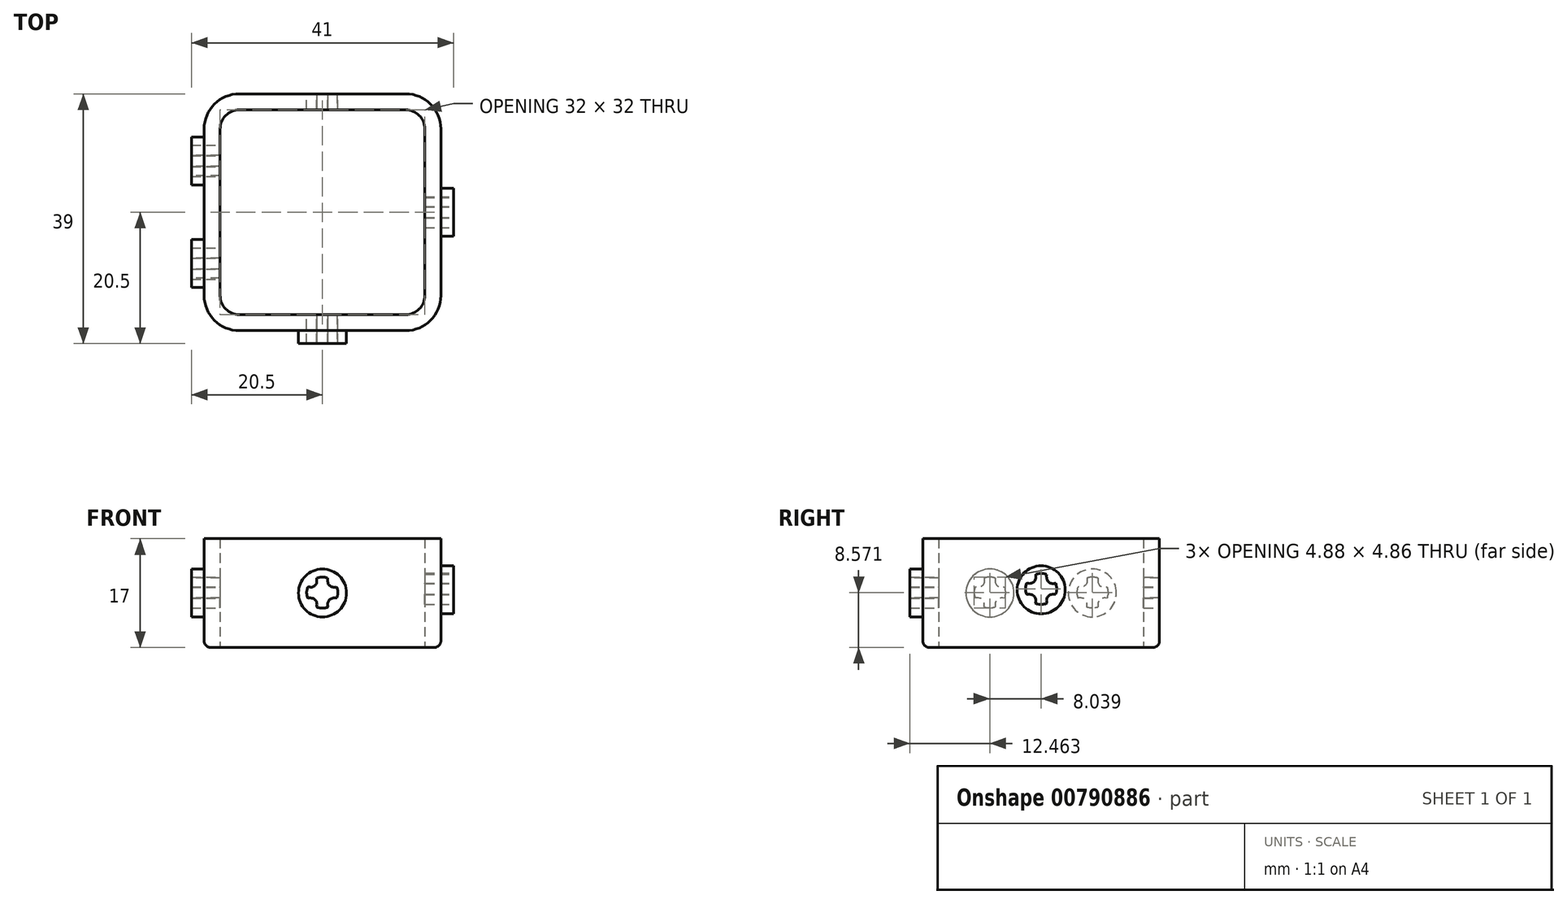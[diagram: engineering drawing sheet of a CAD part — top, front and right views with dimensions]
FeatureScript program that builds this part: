
annotation { "Feature Type Name" : "Feature", "Feature Type Description" : "" }
export const myFeature = defineFeature(function(context is Context, id is Id, definition is map)
    precondition{}
    {
        {
            var Q0;
            Q0=qCreatedBy(makeId("Top.planeOp"),FACE);
            var sketch = newSketch(context, id + "F0", { "sketchPlane" : qUnion([Q0])});
            skLineSegment(sketch, "E0.bottom", {"start": v(-16, 16) * mm, "end": v(16, 16) * mm});
            skLineSegment(sketch, "E0.top", {"start": v(-16, -16) * mm, "end": v(16, -16) * mm});
            skLineSegment(sketch, "E0.left", {"start": v(-16, 16) * mm, "end": v(-16, -16) * mm});
            skLineSegment(sketch, "E0.right", {"start": v(16, 16) * mm, "end": v(16, -16) * mm});
            skPoint(sketch, "E1", {"position": v(-16, 0) * mm});
            skPoint(sketch, "E2", {"position": v(0, 16) * mm});
            skLineSegment(sketch, "E3.bottom", {"start": v(-18.5, 18.5) * mm, "end": v(18.5, 18.5) * mm});
            skLineSegment(sketch, "E3.top", {"start": v(-18.5, -18.5) * mm, "end": v(18.5, -18.5) * mm});
            skLineSegment(sketch, "E3.left", {"start": v(-18.5, 18.5) * mm, "end": v(-18.5, -18.5) * mm});
            skLineSegment(sketch, "E3.right", {"start": v(18.5, 18.5) * mm, "end": v(18.5, -18.5) * mm});
            skSolve(sketch);
        }
        {
            var Q0;
            Q0=makeQuery(id+"F0.imprint","IMPRINT",FACE,{"disambiguationData":[TD([[makeQuery(id+"F0.imprint","IMPRINT",EDGE,{"derivedFrom":sQuery(id+"F0.wireOp",EDGE,"E0.bottom")}),1.0]])]});
            extrude(context, id + "F1", {"entities" : qUnion([Q0]), "depth" : 17 * mm, "offsetDistance" : 25 * mm});
        }
        {
            var Q0;
            Q0=makeQuery(id+"F1.opExtrude","SWEPT_EDGE",EDGE,{"disambiguationData":[OSD([sQuery(id+"F0.wireOp",EDGE,"E0.bottom"),sQuery(id+"F0.wireOp",EDGE,"E0.left")])]});
            var Q1;
            Q1=makeQuery(id+"F1.opExtrude","SWEPT_EDGE",EDGE,{"disambiguationData":[OSD([sQuery(id+"F0.wireOp",EDGE,"E0.bottom"),sQuery(id+"F0.wireOp",EDGE,"E0.right")])]});
            var Q2;
            Q2=makeQuery(id+"F1.opExtrude","SWEPT_EDGE",EDGE,{"disambiguationData":[OSD([sQuery(id+"F0.wireOp",EDGE,"E0.top"),sQuery(id+"F0.wireOp",EDGE,"E0.right")])]});
            var Q3;
            Q3=makeQuery(id+"F1.opExtrude","SWEPT_EDGE",EDGE,{"disambiguationData":[OSD([sQuery(id+"F0.wireOp",EDGE,"E0.top"),sQuery(id+"F0.wireOp",EDGE,"E0.left")])]});
            fillet(context, id + "F2", {"entities" : qUnion([Q0, Q1, Q2, Q3]), "radius" : 3 * mm, "tangentPropagation" : true, "allowEdgeOverflow" : false});
        }
        {
            var Q0;
            Q0=makeQuery(id+"F1.opExtrude","SWEPT_FACE",FACE,{"disambiguationData":[OSD([sQuery(id+"F0.wireOp",EDGE,"E3.left")])]});
            var sketch = newSketch(context, id + "F3", { "sketchPlane" : qUnion([Q0])});
            skCircle(sketch, "E4", {"center": v(-8, 8.5) * mm, "radius": 3.75 * mm});
            skCircle(sketch, "E5", {"center": v(8, 8.5) * mm, "radius": 3.75 * mm});
            skLineSegment(sketch, "E6", {"start": v(-8, 8.5) * mm, "end": v(8, 8.5) * mm});
            skPoint(sketch, "E7", {"position": v(0, 8.5) * mm});
            skSolve(sketch);
        }
        {
            var Q0;
            Q0=makeQuery(id+"F3.imprint","IMPRINT",FACE,{"disambiguationData":[TD([[makeQuery(id+"F3.imprint","IMPRINT",EDGE,{"derivedFrom":sQuery(id+"F3.wireOp",EDGE,"E4")}),1.0]])]});
            var Q1;
            Q1=makeQuery(id+"F3.imprint","IMPRINT",FACE,{"disambiguationData":[TD([[makeQuery(id+"F3.imprint","IMPRINT",EDGE,{"derivedFrom":sQuery(id+"F3.wireOp",EDGE,"ysG9YYlj-4qmX-fUi1-GXW1-Whetp2Y7ZTwk")}),1.0]])]});
            var Q2;
            Q2=makeQuery(id+"F3.imprint","IMPRINT",FACE,{"disambiguationData":[TD([[makeQuery(id+"F3.imprint","IMPRINT",EDGE,{"derivedFrom":sQuery(id+"F3.wireOp",EDGE,"E5")}),1.0]])]});
            extrude(context, id + "F4", {"entities" : qUnion([Q0, Q1, Q2]), "operationType" : NewBodyOperationType.ADD, "depth" : 2 * mm, "offsetDistance" : 25 * mm});
        }
        {
            var Q0;
            Q0=makeQuery(id+"F1.opExtrude","SWEPT_FACE",FACE,{"disambiguationData":[OSD([sQuery(id+"F0.wireOp",EDGE,"E3.top")])]});
            var sketch = newSketch(context, id + "F5", { "sketchPlane" : qUnion([Q0])});
            skCircle(sketch, "E8", {"center": v(0, 8.5) * mm, "radius": 3.75 * mm});
            skSolve(sketch);
        }
        {
            var Q0;
            Q0=makeQuery(id+"F5.imprint","IMPRINT",FACE,{"disambiguationData":[TD([[makeQuery(id+"F5.imprint","IMPRINT",EDGE,{"derivedFrom":sQuery(id+"F5.wireOp",EDGE,"E8")}),1.0]])]});
            extrude(context, id + "F6", {"entities" : qUnion([Q0]), "operationType" : NewBodyOperationType.ADD, "depth" : 2 * mm, "offsetDistance" : 25 * mm});
        }
        {
            var Q0;
            Q0=makeQuery(id+"F6.opExtrude","CAP_FACE",FACE,{"disambiguationData":[OSD([sQuery(id+"F5.wireOp",EDGE,"E8")])],"isStart":false});
            var sketch = newSketch(context, id + "F7", { "sketchPlane" : qUnion([Q0])});
            skFitSpline(sketch, "E9", {"points": [v(-0.88, 10.83) * mm, v(0, 11) * mm, v(0.82, 10.83) * mm], "startDerivative": vector(1.75, 0.5) * mm, "endDerivative": vector(1.65, -0.5) * mm});
            skFitSpline(sketch, "E10", {"points": [v(0.82, 10.83) * mm, v(0.82, 10.27) * mm, v(0.97, 9.83) * mm, v(1.28, 9.54) * mm, v(1.62, 9.42) * mm, v(2.04, 9.41) * mm, v(2.24, 9.41) * mm, v(2.32, 9.17) * mm, v(2.4, 8.78) * mm, v(2.4, 8.44) * mm, v(2.36, 8.13) * mm, v(2.24, 7.71) * mm], "startDerivative": vector(-0.26, -5.18) * mm, "endDerivative": vector(-1.41, -4.37) * mm});
            skFitSpline(sketch, "E11", {"points": [v(-0.88, 10.83) * mm, v(-0.88, 10.54) * mm, v(-0.88, 10.3) * mm, v(-0.91, 10.1) * mm, v(-1.08, 9.76) * mm, v(-1.28, 9.58) * mm, v(-1.54, 9.45) * mm, v(-1.86, 9.41) * mm, v(-2.3, 9.41) * mm, v(-2.4, 9.13) * mm, v(-2.45, 8.85) * mm, v(-2.47, 8.52) * mm, v(-2.44, 8.23) * mm, v(-2.38, 7.96) * mm, v(-2.3, 7.71) * mm, v(-2.1, 7.71) * mm, v(-1.8, 7.71) * mm, v(-1.55, 7.68) * mm, v(-1.36, 7.6) * mm, v(-1.13, 7.42) * mm, v(-1.03, 7.28) * mm, v(-0.94, 7.1) * mm, v(-0.88, 6.86) * mm, v(-0.88, 6.6) * mm, v(-0.88, 6.3) * mm, v(-0.63, 6.21) * mm, v(-0.28, 6.15) * mm, v(0, 6.14) * mm, v(0.27, 6.16) * mm, v(0.63, 6.23) * mm, v(0.82, 6.3) * mm, v(0.82, 6.6) * mm, v(0.82, 6.89) * mm, v(0.92, 7.22) * mm, v(1.06, 7.41) * mm, v(1.33, 7.61) * mm, v(1.74, 7.71) * mm, v(2.24, 7.71) * mm], "startDerivative": vector(-0.02, -10.87) * mm, "endDerivative": vector(14.17, -0.52) * mm});
            skLineSegment(sketch, "E12", {"start": v(0, 11) * mm, "end": v(0, 6.14) * mm});
            skPoint(sketch, "E13", {"position": v(0, 8.57) * mm});
            skPoint(sketch, "E14", {"position": v(0, 8.36) * mm});
            skLineSegment(sketch, "E15", {"start": v(-2.47, 8.52) * mm, "end": v(2.42, 8.52) * mm});
            skSolve(sketch);
        }
        {
            var Q0;
            {var subQ0=sQuery(id+"F7.wireOp",EDGE,"E11");var subQ1=sQuery(id+"F7.wireOp",EDGE,"E9");var subQ2=makeQuery(id+"F7.imprint","INTERSECT",VERTEX,{"derivedFrom":[subQ1,subQ0]});Q0=makeQuery(id+"F7.imprint","IMPRINT",FACE,{"disambiguationData":[TD([[makeQuery(id+"F7.imprint","IMPRINT",EDGE,{"disambiguationData":[TD([[subQ2,-1.0]])],"derivedFrom":subQ1}),-1.0]])]});}
            var Q1;
            {var subQ0=sQuery(id+"F7.wireOp",EDGE,"E10");var subQ1=sQuery(id+"F7.wireOp",EDGE,"E9");var subQ2=makeQuery(id+"F7.imprint","INTERSECT",VERTEX,{"derivedFrom":[subQ1,subQ0]});Q1=makeQuery(id+"F7.imprint","IMPRINT",FACE,{"disambiguationData":[TD([[makeQuery(id+"F7.imprint","IMPRINT",EDGE,{"disambiguationData":[TD([[subQ2,1.0]])],"derivedFrom":subQ1}),-1.0]])]});}
            var Q2;
            {var subQ0=sQuery(id+"F7.wireOp",EDGE,"E11");var subQ1=sQuery(id+"F7.wireOp",EDGE,"E10");var subQ2=makeQuery(id+"F7.imprint","INTERSECT",VERTEX,{"derivedFrom":[subQ1,subQ0]});Q2=makeQuery(id+"F7.imprint","IMPRINT",FACE,{"disambiguationData":[TD([[makeQuery(id+"F7.imprint","IMPRINT",EDGE,{"disambiguationData":[TD([[subQ2,1.0]])],"derivedFrom":subQ1}),-1.0]])]});}
            var Q3;
            {var subQ0=sQuery(id+"F7.wireOp",EDGE,"E12");var subQ1=sQuery(id+"F7.wireOp",EDGE,"E11");var subQ2=makeQuery(id+"F7.imprint","INTERSECT",VERTEX,{"derivedFrom":[subQ1,subQ0]});Q3=makeQuery(id+"F7.imprint","IMPRINT",FACE,{"disambiguationData":[TD([[makeQuery(id+"F7.imprint","IMPRINT",EDGE,{"disambiguationData":[TD([[subQ2,1.0]])],"derivedFrom":subQ1}),1.0]])]});}
            extrude(context, id + "F8", {"entities" : qUnion([Q0, Q1, Q2, Q3]), "operationType" : NewBodyOperationType.REMOVE, "oppositeDirection" : true, "depth" : 43.1 * mm, "offsetDistance" : 25 * mm});
        }
        {
            var Q0;
            Q0=makeQuery(id+"F1.opExtrude","SWEPT_EDGE",EDGE,{"disambiguationData":[OSD([sQuery(id+"F0.wireOp",EDGE,"E3.top"),sQuery(id+"F0.wireOp",EDGE,"E3.left")])]});
            var Q1;
            Q1=makeQuery(id+"F1.opExtrude","SWEPT_EDGE",EDGE,{"disambiguationData":[OSD([sQuery(id+"F0.wireOp",EDGE,"E3.top"),sQuery(id+"F0.wireOp",EDGE,"E3.right")])]});
            var Q2;
            Q2=makeQuery(id+"F1.opExtrude","SWEPT_EDGE",EDGE,{"disambiguationData":[OSD([sQuery(id+"F0.wireOp",EDGE,"E3.bottom"),sQuery(id+"F0.wireOp",EDGE,"E3.right")])]});
            var Q3;
            Q3=makeQuery(id+"F1.opExtrude","SWEPT_EDGE",EDGE,{"disambiguationData":[OSD([sQuery(id+"F0.wireOp",EDGE,"E3.bottom"),sQuery(id+"F0.wireOp",EDGE,"E3.left")])]});
            fillet(context, id + "F9", {"entities" : qUnion([Q0, Q1, Q2, Q3]), "radius" : 5.5 * mm, "tangentPropagation" : true, "allowEdgeOverflow" : false});
        }
        {
            var Q0;
            Q0=makeQuery(id+"F1.opExtrude","CAP_EDGE",EDGE,{"disambiguationData":[OSD([sQuery(id+"F0.wireOp",EDGE,"E3.right")])],"isStart":true});
            var Q1;
            {var subQ0=sQuery(id+"F0.wireOp",EDGE,"E3.left");var subQ1=sQuery(id+"F0.wireOp",EDGE,"E3.top");Q1=makeQuery(id+"F9.opFillet","BLEND_EDGE",EDGE,{"blendedFrom":[makeQuery(id+"F1.opExtrude","SWEPT_EDGE",EDGE,{"disambiguationData":[OSD([subQ1,subQ0])]}),makeQuery(id+"F1.opExtrude","CAP_FACE",FACE,{"disambiguationData":[OSD([sQuery(id+"F0.wireOp",EDGE,"E0.bottom"),sQuery(id+"F0.wireOp",EDGE,"E0.top"),sQuery(id+"F0.wireOp",EDGE,"E0.left"),sQuery(id+"F0.wireOp",EDGE,"E0.right"),sQuery(id+"F0.wireOp",EDGE,"E3.bottom"),subQ1,subQ0,sQuery(id+"F0.wireOp",EDGE,"E3.right")])],"isStart":true})],"blendedInto":[makeQuery(id+"F1.opExtrude","CAP_FACE",FACE,{"disambiguationData":[OSD([sQuery(id+"F0.wireOp",EDGE,"E0.bottom"),sQuery(id+"F0.wireOp",EDGE,"E0.top"),sQuery(id+"F0.wireOp",EDGE,"E0.left"),sQuery(id+"F0.wireOp",EDGE,"E0.right"),sQuery(id+"F0.wireOp",EDGE,"E3.bottom"),subQ1,subQ0,sQuery(id+"F0.wireOp",EDGE,"E3.right")])],"isStart":true})]});}
            var Q2;
            Q2=makeQuery(id+"F1.opExtrude","CAP_EDGE",EDGE,{"disambiguationData":[OSD([sQuery(id+"F0.wireOp",EDGE,"E3.top")])],"isStart":true});
            var Q3;
            {var subQ0=sQuery(id+"F0.wireOp",EDGE,"E3.right");var subQ1=sQuery(id+"F0.wireOp",EDGE,"E3.top");Q3=makeQuery(id+"F9.opFillet","BLEND_EDGE",EDGE,{"blendedFrom":[makeQuery(id+"F1.opExtrude","SWEPT_EDGE",EDGE,{"disambiguationData":[OSD([subQ1,subQ0])]}),makeQuery(id+"F1.opExtrude","CAP_FACE",FACE,{"disambiguationData":[OSD([sQuery(id+"F0.wireOp",EDGE,"E0.bottom"),sQuery(id+"F0.wireOp",EDGE,"E0.top"),sQuery(id+"F0.wireOp",EDGE,"E0.left"),sQuery(id+"F0.wireOp",EDGE,"E0.right"),sQuery(id+"F0.wireOp",EDGE,"E3.bottom"),subQ1,sQuery(id+"F0.wireOp",EDGE,"E3.left"),subQ0])],"isStart":true})],"blendedInto":[makeQuery(id+"F1.opExtrude","CAP_FACE",FACE,{"disambiguationData":[OSD([sQuery(id+"F0.wireOp",EDGE,"E0.bottom"),sQuery(id+"F0.wireOp",EDGE,"E0.top"),sQuery(id+"F0.wireOp",EDGE,"E0.left"),sQuery(id+"F0.wireOp",EDGE,"E0.right"),sQuery(id+"F0.wireOp",EDGE,"E3.bottom"),subQ1,sQuery(id+"F0.wireOp",EDGE,"E3.left"),subQ0])],"isStart":true})]});}
            var Q4;
            Q4=makeQuery(id+"F1.opExtrude","CAP_EDGE",EDGE,{"disambiguationData":[OSD([sQuery(id+"F0.wireOp",EDGE,"E3.left")])],"isStart":true});
            var Q5;
            {var subQ0=sQuery(id+"F0.wireOp",EDGE,"E3.left");var subQ1=sQuery(id+"F0.wireOp",EDGE,"E3.bottom");Q5=makeQuery(id+"F9.opFillet","BLEND_EDGE",EDGE,{"blendedFrom":[makeQuery(id+"F1.opExtrude","SWEPT_EDGE",EDGE,{"disambiguationData":[OSD([subQ1,subQ0])]}),makeQuery(id+"F1.opExtrude","CAP_FACE",FACE,{"disambiguationData":[OSD([sQuery(id+"F0.wireOp",EDGE,"E0.bottom"),sQuery(id+"F0.wireOp",EDGE,"E0.top"),sQuery(id+"F0.wireOp",EDGE,"E0.left"),sQuery(id+"F0.wireOp",EDGE,"E0.right"),subQ1,sQuery(id+"F0.wireOp",EDGE,"E3.top"),subQ0,sQuery(id+"F0.wireOp",EDGE,"E3.right")])],"isStart":true})],"blendedInto":[makeQuery(id+"F1.opExtrude","CAP_FACE",FACE,{"disambiguationData":[OSD([sQuery(id+"F0.wireOp",EDGE,"E0.bottom"),sQuery(id+"F0.wireOp",EDGE,"E0.top"),sQuery(id+"F0.wireOp",EDGE,"E0.left"),sQuery(id+"F0.wireOp",EDGE,"E0.right"),subQ1,sQuery(id+"F0.wireOp",EDGE,"E3.top"),subQ0,sQuery(id+"F0.wireOp",EDGE,"E3.right")])],"isStart":true})]});}
            var Q6;
            Q6=makeQuery(id+"F1.opExtrude","CAP_EDGE",EDGE,{"disambiguationData":[OSD([sQuery(id+"F0.wireOp",EDGE,"E3.bottom")])],"isStart":true});
            var Q7;
            {var subQ0=sQuery(id+"F0.wireOp",EDGE,"E3.right");var subQ1=sQuery(id+"F0.wireOp",EDGE,"E3.bottom");Q7=makeQuery(id+"F9.opFillet","BLEND_EDGE",EDGE,{"blendedFrom":[makeQuery(id+"F1.opExtrude","SWEPT_EDGE",EDGE,{"disambiguationData":[OSD([subQ1,subQ0])]}),makeQuery(id+"F1.opExtrude","CAP_FACE",FACE,{"disambiguationData":[OSD([sQuery(id+"F0.wireOp",EDGE,"E0.bottom"),sQuery(id+"F0.wireOp",EDGE,"E0.top"),sQuery(id+"F0.wireOp",EDGE,"E0.left"),sQuery(id+"F0.wireOp",EDGE,"E0.right"),subQ1,sQuery(id+"F0.wireOp",EDGE,"E3.top"),sQuery(id+"F0.wireOp",EDGE,"E3.left"),subQ0])],"isStart":true})],"blendedInto":[makeQuery(id+"F1.opExtrude","CAP_FACE",FACE,{"disambiguationData":[OSD([sQuery(id+"F0.wireOp",EDGE,"E0.bottom"),sQuery(id+"F0.wireOp",EDGE,"E0.top"),sQuery(id+"F0.wireOp",EDGE,"E0.left"),sQuery(id+"F0.wireOp",EDGE,"E0.right"),subQ1,sQuery(id+"F0.wireOp",EDGE,"E3.top"),sQuery(id+"F0.wireOp",EDGE,"E3.left"),subQ0])],"isStart":true})]});}
            fillet(context, id + "F10", {"entities" : qUnion([Q0, Q1, Q2, Q3, Q4, Q5, Q6, Q7]), "radius" : 1 * mm, "tangentPropagation" : true, "allowEdgeOverflow" : false});
        }
        {
            var Q0;
            Q0=makeQuery(id+"F4.opExtrude","CAP_FACE",FACE,{"disambiguationData":[OSD([sQuery(id+"F3.wireOp",EDGE,"E4")])],"isStart":false});
            var sketch = newSketch(context, id + "F11", { "sketchPlane" : qUnion([Q0])});
            skFitSpline(sketch, "E16", {"points": [v(-8.86, 10.84) * mm, v(-7.98, 11) * mm, v(-7.16, 10.84) * mm], "startDerivative": vector(1.75, 0.5) * mm, "endDerivative": vector(1.65, -0.5) * mm});
            skFitSpline(sketch, "E17", {"points": [v(-7.16, 10.84) * mm, v(-7.16, 10.27) * mm, v(-7.02, 9.84) * mm, v(-6.7, 9.54) * mm, v(-6.36, 9.42) * mm, v(-5.94, 9.41) * mm, v(-5.74, 9.41) * mm, v(-5.66, 9.17) * mm, v(-5.59, 8.79) * mm, v(-5.58, 8.45) * mm, v(-5.62, 8.13) * mm, v(-5.74, 7.71) * mm], "startDerivative": vector(-0.26, -5.18) * mm, "endDerivative": vector(-1.41, -4.37) * mm});
            skFitSpline(sketch, "E18", {"points": [v(-8.86, 10.84) * mm, v(-8.86, 10.54) * mm, v(-8.87, 10.3) * mm, v(-8.9, 10.1) * mm, v(-9.07, 9.76) * mm, v(-9.26, 9.58) * mm, v(-9.52, 9.45) * mm, v(-9.84, 9.41) * mm, v(-10.29, 9.41) * mm, v(-10.37, 9.14) * mm, v(-10.43, 8.85) * mm, v(-10.45, 8.52) * mm, v(-10.43, 8.23) * mm, v(-10.37, 7.97) * mm, v(-10.29, 7.71) * mm, v(-10.1, 7.71) * mm, v(-9.78, 7.71) * mm, v(-9.53, 7.68) * mm, v(-9.34, 7.6) * mm, v(-9.12, 7.42) * mm, v(-9, 7.28) * mm, v(-8.92, 7.1) * mm, v(-8.87, 6.86) * mm, v(-8.86, 6.61) * mm, v(-8.86, 6.3) * mm, v(-8.6, 6.21) * mm, v(-8.26, 6.15) * mm, v(-7.98, 6.14) * mm, v(-7.72, 6.16) * mm, v(-7.35, 6.23) * mm, v(-7.16, 6.3) * mm, v(-7.16, 6.61) * mm, v(-7.16, 6.89) * mm, v(-7.06, 7.22) * mm, v(-6.92, 7.41) * mm, v(-6.65, 7.62) * mm, v(-6.24, 7.71) * mm, v(-5.74, 7.71) * mm], "startDerivative": vector(-0.02, -10.87) * mm, "endDerivative": vector(14.17, -0.52) * mm});
            skLineSegment(sketch, "E19", {"start": v(-7.98, 11) * mm, "end": v(-7.98, 6.14) * mm});
            skPoint(sketch, "E20", {"position": v(-7.98, 8.57) * mm});
            skPoint(sketch, "E21", {"position": v(-7.98, 8.36) * mm});
            skLineSegment(sketch, "E22", {"start": v(-10.45, 8.52) * mm, "end": v(-5.56, 8.52) * mm});
            skFitSpline(sketch, "E23", {"points": [v(7.19, 10.84) * mm, v(8.07, 11) * mm, v(8.89, 10.84) * mm], "startDerivative": vector(1.75, 0.5) * mm, "endDerivative": vector(1.65, -0.5) * mm});
            skFitSpline(sketch, "E24", {"points": [v(8.89, 10.84) * mm, v(8.89, 10.27) * mm, v(9.04, 9.84) * mm, v(9.35, 9.54) * mm, v(9.7, 9.42) * mm, v(10.1, 9.41) * mm, v(10.3, 9.41) * mm, v(10.39, 9.17) * mm, v(10.46, 8.79) * mm, v(10.47, 8.45) * mm, v(10.43, 8.13) * mm, v(10.3, 7.71) * mm], "startDerivative": vector(-0.26, -5.18) * mm, "endDerivative": vector(-1.41, -4.37) * mm});
            skFitSpline(sketch, "E25", {"points": [v(7.19, 10.84) * mm, v(7.19, 10.54) * mm, v(7.19, 10.3) * mm, v(7.16, 10.1) * mm, v(6.99, 9.76) * mm, v(6.79, 9.58) * mm, v(6.53, 9.45) * mm, v(6.2, 9.41) * mm, v(5.77, 9.41) * mm, v(5.68, 9.14) * mm, v(5.62, 8.85) * mm, v(5.6, 8.52) * mm, v(5.63, 8.23) * mm, v(5.69, 7.97) * mm, v(5.77, 7.71) * mm, v(5.96, 7.71) * mm, v(6.28, 7.71) * mm, v(6.52, 7.68) * mm, v(6.71, 7.6) * mm, v(6.94, 7.42) * mm, v(7.04, 7.28) * mm, v(7.13, 7.1) * mm, v(7.18, 6.86) * mm, v(7.19, 6.61) * mm, v(7.19, 6.3) * mm, v(7.44, 6.21) * mm, v(7.8, 6.15) * mm, v(8.07, 6.14) * mm, v(8.34, 6.16) * mm, v(8.7, 6.23) * mm, v(8.89, 6.3) * mm, v(8.89, 6.61) * mm, v(8.9, 6.89) * mm, v(9, 7.22) * mm, v(9.13, 7.41) * mm, v(9.4, 7.62) * mm, v(9.81, 7.71) * mm, v(10.3, 7.71) * mm], "startDerivative": vector(-0.02, -10.87) * mm, "endDerivative": vector(14.17, -0.52) * mm});
            skLineSegment(sketch, "E26", {"start": v(8.07, 11) * mm, "end": v(8.07, 6.14) * mm});
            skPoint(sketch, "E27", {"position": v(8.07, 8.57) * mm});
            skPoint(sketch, "E28", {"position": v(8.07, 8.36) * mm});
            skLineSegment(sketch, "E29", {"start": v(5.6, 8.52) * mm, "end": v(10.49, 8.52) * mm});
            skSolve(sketch);
        }
        {
            var Q0;
            {var subQ0=sQuery(id+"F11.wireOp",EDGE,"E18");var subQ1=sQuery(id+"F11.wireOp",EDGE,"E16");var subQ2=makeQuery(id+"F11.imprint","INTERSECT",VERTEX,{"derivedFrom":[subQ1,subQ0]});Q0=makeQuery(id+"F11.imprint","IMPRINT",FACE,{"disambiguationData":[TD([[makeQuery(id+"F11.imprint","IMPRINT",EDGE,{"disambiguationData":[TD([[subQ2,-1.0]])],"derivedFrom":subQ1}),-1.0]])]});}
            var Q1;
            {var subQ0=sQuery(id+"F11.wireOp",EDGE,"E17");var subQ1=sQuery(id+"F11.wireOp",EDGE,"E16");var subQ2=makeQuery(id+"F11.imprint","INTERSECT",VERTEX,{"derivedFrom":[subQ1,subQ0]});Q1=makeQuery(id+"F11.imprint","IMPRINT",FACE,{"disambiguationData":[TD([[makeQuery(id+"F11.imprint","IMPRINT",EDGE,{"disambiguationData":[TD([[subQ2,1.0]])],"derivedFrom":subQ1}),-1.0]])]});}
            var Q2;
            {var subQ0=sQuery(id+"F11.wireOp",EDGE,"E18");var subQ1=sQuery(id+"F11.wireOp",EDGE,"E17");var subQ2=makeQuery(id+"F11.imprint","INTERSECT",VERTEX,{"derivedFrom":[subQ1,subQ0]});Q2=makeQuery(id+"F11.imprint","IMPRINT",FACE,{"disambiguationData":[TD([[makeQuery(id+"F11.imprint","IMPRINT",EDGE,{"disambiguationData":[TD([[subQ2,1.0]])],"derivedFrom":subQ1}),-1.0]])]});}
            var Q3;
            {var subQ0=sQuery(id+"F11.wireOp",EDGE,"E19");var subQ1=sQuery(id+"F11.wireOp",EDGE,"E18");var subQ2=makeQuery(id+"F11.imprint","INTERSECT",VERTEX,{"derivedFrom":[subQ1,subQ0]});Q3=makeQuery(id+"F11.imprint","IMPRINT",FACE,{"disambiguationData":[TD([[makeQuery(id+"F11.imprint","IMPRINT",EDGE,{"disambiguationData":[TD([[subQ2,1.0]])],"derivedFrom":subQ1}),1.0]])]});}
            var Q4;
            {var subQ0=sQuery(id+"F11.wireOp",EDGE,"E25");var subQ1=sQuery(id+"F11.wireOp",EDGE,"E23");var subQ2=makeQuery(id+"F11.imprint","INTERSECT",VERTEX,{"derivedFrom":[subQ1,subQ0]});Q4=makeQuery(id+"F11.imprint","IMPRINT",FACE,{"disambiguationData":[TD([[makeQuery(id+"F11.imprint","IMPRINT",EDGE,{"disambiguationData":[TD([[subQ2,-1.0]])],"derivedFrom":subQ1}),-1.0]])]});}
            var Q5;
            {var subQ0=sQuery(id+"F11.wireOp",EDGE,"E24");var subQ1=sQuery(id+"F11.wireOp",EDGE,"E23");var subQ2=makeQuery(id+"F11.imprint","INTERSECT",VERTEX,{"derivedFrom":[subQ1,subQ0]});Q5=makeQuery(id+"F11.imprint","IMPRINT",FACE,{"disambiguationData":[TD([[makeQuery(id+"F11.imprint","IMPRINT",EDGE,{"disambiguationData":[TD([[subQ2,1.0]])],"derivedFrom":subQ1}),-1.0]])]});}
            var Q6;
            {var subQ0=sQuery(id+"F11.wireOp",EDGE,"E25");var subQ1=sQuery(id+"F11.wireOp",EDGE,"E24");var subQ2=makeQuery(id+"F11.imprint","INTERSECT",VERTEX,{"derivedFrom":[subQ1,subQ0]});Q6=makeQuery(id+"F11.imprint","IMPRINT",FACE,{"disambiguationData":[TD([[makeQuery(id+"F11.imprint","IMPRINT",EDGE,{"disambiguationData":[TD([[subQ2,1.0]])],"derivedFrom":subQ1}),-1.0]])]});}
            var Q7;
            {var subQ0=sQuery(id+"F11.wireOp",EDGE,"E26");var subQ1=sQuery(id+"F11.wireOp",EDGE,"E25");var subQ2=makeQuery(id+"F11.imprint","INTERSECT",VERTEX,{"derivedFrom":[subQ1,subQ0]});Q7=makeQuery(id+"F11.imprint","IMPRINT",FACE,{"disambiguationData":[TD([[makeQuery(id+"F11.imprint","IMPRINT",EDGE,{"disambiguationData":[TD([[subQ2,1.0]])],"derivedFrom":subQ1}),1.0]])]});}
            extrude(context, id + "F12", {"entities" : qUnion([Q0, Q1, Q2, Q3, Q4, Q5, Q6, Q7]), "operationType" : NewBodyOperationType.REMOVE, "oppositeDirection" : true, "depth" : 19.1 * mm, "offsetDistance" : 25 * mm});
        }
        {
            var Q0;
            Q0=makeQuery(id+"F1.opExtrude","SWEPT_FACE",FACE,{"disambiguationData":[OSD([sQuery(id+"F0.wireOp",EDGE,"E3.right")])]});
            var sketch = newSketch(context, id + "F13", { "sketchPlane" : qUnion([Q0])});
            skCircle(sketch, "E30", {"center": v(0, 9) * mm, "radius": 3.75 * mm});
            skSolve(sketch);
        }
        {
            var Q0;
            Q0=makeQuery(id+"F13.imprint","IMPRINT",FACE,{"disambiguationData":[TD([[makeQuery(id+"F13.imprint","IMPRINT",EDGE,{"derivedFrom":sQuery(id+"F13.wireOp",EDGE,"E30")}),1.0]])]});
            extrude(context, id + "F14", {"entities" : qUnion([Q0]), "operationType" : NewBodyOperationType.ADD, "depth" : 2 * mm, "offsetDistance" : 25 * mm});
        }
        {
            var Q0;
            Q0=makeQuery(id+"F14.opExtrude","CAP_FACE",FACE,{"disambiguationData":[OSD([sQuery(id+"F13.wireOp",EDGE,"E30")])],"isStart":false});
            var sketch = newSketch(context, id + "F15", { "sketchPlane" : qUnion([Q0])});
            skFitSpline(sketch, "E31", {"points": [v(-0.85, 11.42) * mm, v(0.04, 11.58) * mm, v(0.85, 11.42) * mm], "startDerivative": vector(1.75, 0.5) * mm, "endDerivative": vector(1.65, -0.5) * mm});
            skFitSpline(sketch, "E32", {"points": [v(0.85, 11.42) * mm, v(0.85, 10.85) * mm, v(1, 10.42) * mm, v(1.32, 10.12) * mm, v(1.66, 10) * mm, v(2.07, 10) * mm, v(2.27, 10) * mm, v(2.35, 9.75) * mm, v(2.43, 9.37) * mm, v(2.44, 9.03) * mm, v(2.4, 8.7) * mm, v(2.27, 8.3) * mm], "startDerivative": vector(-0.26, -5.18) * mm, "endDerivative": vector(-1.41, -4.37) * mm});
            skFitSpline(sketch, "E33", {"points": [v(-0.85, 11.42) * mm, v(-0.85, 11.12) * mm, v(-0.85, 10.87) * mm, v(-0.88, 10.68) * mm, v(-1.05, 10.34) * mm, v(-1.25, 10.16) * mm, v(-1.5, 10.03) * mm, v(-1.83, 10) * mm, v(-2.27, 10) * mm, v(-2.36, 9.72) * mm, v(-2.42, 9.43) * mm, v(-2.44, 9.1) * mm, v(-2.4, 8.81) * mm, v(-2.35, 8.55) * mm, v(-2.27, 8.3) * mm, v(-2.08, 8.3) * mm, v(-1.76, 8.3) * mm, v(-1.51, 8.26) * mm, v(-1.32, 8.18) * mm, v(-1.1, 8) * mm, v(-1, 7.87) * mm, v(-0.9, 7.69) * mm, v(-0.85, 7.44) * mm, v(-0.85, 7.2) * mm, v(-0.85, 6.87) * mm, v(-0.6, 6.8) * mm, v(-0.24, 6.73) * mm, v(0.04, 6.72) * mm, v(0.3, 6.74) * mm, v(0.67, 6.81) * mm, v(0.85, 6.87) * mm, v(0.85, 7.2) * mm, v(0.86, 7.47) * mm, v(0.96, 7.8) * mm, v(1.1, 8) * mm, v(1.36, 8.2) * mm, v(1.78, 8.3) * mm, v(2.27, 8.3) * mm], "startDerivative": vector(-0.02, -10.87) * mm, "endDerivative": vector(14.17, -0.52) * mm});
            skLineSegment(sketch, "E34", {"start": v(0.04, 11.58) * mm, "end": v(0.04, 6.72) * mm});
            skPoint(sketch, "E35", {"position": v(0.04, 9.15) * mm});
            skPoint(sketch, "E36", {"position": v(0.03, 8.94) * mm});
            skLineSegment(sketch, "E37", {"start": v(-2.44, 9.1) * mm, "end": v(2.45, 9.1) * mm});
            skSolve(sketch);
        }
        {
            var Q0;
            {var subQ0=sQuery(id+"F15.wireOp",EDGE,"E33");var subQ1=sQuery(id+"F15.wireOp",EDGE,"E31");var subQ2=makeQuery(id+"F15.imprint","INTERSECT",VERTEX,{"derivedFrom":[subQ1,subQ0]});Q0=makeQuery(id+"F15.imprint","IMPRINT",FACE,{"disambiguationData":[TD([[makeQuery(id+"F15.imprint","IMPRINT",EDGE,{"disambiguationData":[TD([[subQ2,-1.0]])],"derivedFrom":subQ1}),-1.0]])]});}
            var Q1;
            {var subQ0=sQuery(id+"F15.wireOp",EDGE,"E32");var subQ1=sQuery(id+"F15.wireOp",EDGE,"E31");var subQ2=makeQuery(id+"F15.imprint","INTERSECT",VERTEX,{"derivedFrom":[subQ1,subQ0]});Q1=makeQuery(id+"F15.imprint","IMPRINT",FACE,{"disambiguationData":[TD([[makeQuery(id+"F15.imprint","IMPRINT",EDGE,{"disambiguationData":[TD([[subQ2,1.0]])],"derivedFrom":subQ1}),-1.0]])]});}
            var Q2;
            {var subQ0=sQuery(id+"F15.wireOp",EDGE,"E33");var subQ1=sQuery(id+"F15.wireOp",EDGE,"E32");var subQ2=makeQuery(id+"F15.imprint","INTERSECT",VERTEX,{"derivedFrom":[subQ1,subQ0]});Q2=makeQuery(id+"F15.imprint","IMPRINT",FACE,{"disambiguationData":[TD([[makeQuery(id+"F15.imprint","IMPRINT",EDGE,{"disambiguationData":[TD([[subQ2,1.0]])],"derivedFrom":subQ1}),-1.0]])]});}
            var Q3;
            {var subQ0=sQuery(id+"F15.wireOp",EDGE,"E34");var subQ1=sQuery(id+"F15.wireOp",EDGE,"E33");var subQ2=makeQuery(id+"F15.imprint","INTERSECT",VERTEX,{"derivedFrom":[subQ1,subQ0]});Q3=makeQuery(id+"F15.imprint","IMPRINT",FACE,{"disambiguationData":[TD([[makeQuery(id+"F15.imprint","IMPRINT",EDGE,{"disambiguationData":[TD([[subQ2,1.0]])],"derivedFrom":subQ1}),1.0]])]});}
            extrude(context, id + "F16", {"entities" : qUnion([Q0, Q1, Q2, Q3]), "operationType" : NewBodyOperationType.REMOVE, "oppositeDirection" : true, "depth" : 25 * mm, "offsetDistance" : 25 * mm});
        }
    });
